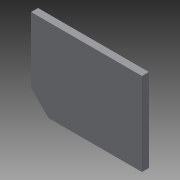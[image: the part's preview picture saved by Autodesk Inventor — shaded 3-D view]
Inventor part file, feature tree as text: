
AUTODESK INVENTOR PART (.ipt)
format: ipt  version: 2014 (Build 180170000, 170)  size: 72,192 bytes
history: native  units: mm
features: extrude x1, sketch x1
ambient origin geometry x8: Origin, YZ Plane, XZ Plane, XY Plane, X Axis, Y Axis, Z Axis, Center Point
bodies: Volumenkörper1 (feature_tree)
feature tree (2):
  extrude  "Extrusion1"  Depth=24.0mm
  sketch  "Skizze1"  dims[d0=32.0mm d1=24.0mm d2=45.0deg d3=19.0mm d4=2.0mm d5=0.0mm]
